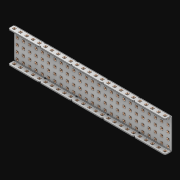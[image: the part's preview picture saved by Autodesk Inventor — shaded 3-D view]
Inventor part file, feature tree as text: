
AUTODESK INVENTOR PART (.ipt)
format: ipt  version: 2021 (Build 250183000, 183)  size: 3,581,952 bytes
history: native  units: in
note: dims shown in document units (in); Inventor stores cm internally (conversion verified against a paired STEP export)
features: extrude x176, other x175, sketch x4, thicken_offset x3, pattern_linear x3, imported_body x1
ambient origin geometry x8: Origin, YZ Plane, XZ Plane, XY Plane, X Axis, Y Axis, Z Axis, Center Point
bodies: Solid1 (feature_tree)
feature tree (362):
  thicken_offset  "Thicken1"
  thicken_offset  "Thicken2"
  thicken_offset  "Thicken3"
  pattern_linear  "Rectangular Pattern1"  Spacing1=0.001in  [1 undecoded]
  pattern_linear  "Rectangular Pattern2"  Spacing1=0.001in  [1 undecoded]
  pattern_linear  "Rectangular Pattern3"  Spacing1=0.182in  [1 undecoded]
  extrude  "Extrusion1"  Depth=0.063in TaperAngle=0.0deg
  sketch  "Sketch1"  dims[d0=0.001in]
  other  "Srf1"
  sketch  "Sketch2"  dims[d1=0.001in]
  other  "Srf2"
  sketch  "Sketch3"  dims[d2=0.001in]
  other  "Srf3"
  other  "Srf4"
  other  "Srf5"
  other  "Srf6"
  other  "Srf7"
  other  "Srf8"
  other  "Srf9"
  other  "Srf10"
  other  "Srf11"
  other  "Srf12"
  other  "Srf13"
  other  "Srf14"
  other  "Srf15"
  other  "Srf16"
  other  "Srf17"
  other  "Srf18"
  other  "Srf19"
  other  "Srf20"
  other  "Srf21"
  other  "Srf22"
  other  "Srf23"
  other  "Srf24"
  other  "Srf25"
  other  "Srf26"
  other  "Srf27"
  other  "Srf38"
  other  "Srf39"
  other  "Srf40"
  other  "Srf41"
  other  "Srf42"
  other  "Srf43"
  other  "Srf44"
  other  "Srf45"
  other  "Srf46"
  other  "Srf47"
  other  "Srf48"
  other  "Srf49"
  other  "Srf50"
  other  "Srf51"
  other  "Srf52"
  other  "Srf53"
  other  "Srf54"
  other  "Srf55"
  other  "Srf56"
  other  "Srf57"
  other  "Srf58"
  other  "Srf59"
  other  "Srf60"
  other  "Srf61"
  other  "Srf72"
  other  "Srf73"
  other  "Srf74"
  other  "Srf75"
  other  "Srf76"
  other  "Srf77"
  other  "Srf78"
  other  "Srf79"
  other  "Srf80"
  other  "Srf81"
  other  "Srf82"
  other  "Srf83"
  other  "Srf84"
  other  "Srf85"
  other  "Srf86"
  other  "Srf87"
  other  "Srf88"
  other  "Srf89"
  other  "Srf90"
  other  "Srf91"
  other  "Srf92"
  other  "Srf93"
  other  "Srf94"
  other  "Srf95"
  other  "Srf106"
  other  "Srf107"
  other  "Srf108"
  other  "Srf109"
  other  "Srf110"
  other  "Srf111"
  other  "Srf112"
  other  "Srf113"
  other  "Srf114"
  other  "Srf115"
  other  "Srf116"
  other  "Srf117"
  other  "Srf118"
  other  "Srf119"
  other  "Srf120"
  other  "Srf121"
  other  "Srf122"
  other  "Srf123"
  other  "Srf124"
  other  "Srf125"
  other  "Srf126"
  other  "Srf127"
  other  "Srf128"
  other  "Srf129"
  other  "Srf130"
  other  "Srf141"
  other  "Srf142"
  other  "Srf143"
  other  "Srf144"
  other  "Srf145"
  other  "Srf146"
  other  "Srf147"
  other  "Srf148"
  other  "Srf149"
  other  "Srf150"
  other  "Srf151"
  other  "Srf152"
  other  "Srf153"
  other  "Srf154"
  other  "Srf155"
  other  "Srf156"
  other  "Srf157"
  other  "Srf158"
  other  "Srf159"
  other  "Srf160"
  other  "Srf161"
  other  "Srf162"
  other  "Srf163"
  other  "Srf164"
  other  "Srf165"
  other  "Srf176"
  other  "Srf177"
  other  "Srf178"
  other  "Srf179"
  other  "Srf180"
  other  "Srf181"
  other  "Srf182"
  other  "Srf183"
  other  "Srf184"
  other  "Srf185"
  other  "Srf186"
  other  "Srf187"
  other  "Srf188"
  other  "Srf189"
  other  "Srf190"
  other  "Srf191"
  other  "Srf192"
  other  "Srf193"
  other  "Srf194"
  other  "Srf195"
  other  "Srf196"
  other  "Srf197"
  other  "Srf198"
  other  "Srf199"
  other  "Srf200"
  other  "Srf211"
  other  "Srf212"
  other  "Srf213"
  other  "Srf214"
  other  "Srf215"
  other  "Srf216"
  other  "Srf217"
  other  "Srf218"
  other  "Srf219"
  other  "Srf220"
  other  "Srf221"
  other  "Srf222"
  other  "Srf223"
  other  "Srf224"
  other  "Srf225"
  other  "Srf226"
  other  "Srf227"
  other  "Srf228"
  other  "Srf229"
  other  "Srf230"
  other  "Srf231"
  other  "Srf232"
  other  "Srf233"
  other  "Srf234"
  other  "Srf235"
  sketch  "Sketch4"  dims[d3=0.001in d4=0.001in d5=0.001in d6=0.182in d7=0.063in d8=0.0in d9=0.182in d10=0.063in d11=0.0in d12=0.182in d13=0.063in d14=0.0in d17=0.5in d18=9.8425in d20=0.5in d21=9.8425in d23=0.5in d24=1.9685in d26=0.5in d27=5.0in d28=0.0in]
  imported_body  "Imported1"
  extrude  "ExtrusionSrf1"  Depth=5.0in
  extrude  "ExtrusionSrf2"  Depth=0.063in TaperAngle=0.0deg
  extrude  "ExtrusionSrf3"  Depth=5.0in
  extrude  "ExtrusionSrf4"  Depth=0.063in TaperAngle=0.0deg
  extrude  "ExtrusionSrf5"  Depth=0.5in
  extrude  "ExtrusionSrf6"  Depth=5.0in
  extrude  "ExtrusionSrf7"  Depth=0.5in
  extrude  "ExtrusionSrf8"  Depth=5.0in
  extrude  "ExtrusionSrf9"  Depth=0.5in
  extrude  "ExtrusionSrf10"  Depth=0.5in
  extrude  "ExtrusionSrf11"  Depth=5.0in
  extrude  "ExtrusionSrf12"  TaperAngle=0.0deg  [1 undecoded]
  extrude  "ExtrusionSrf13"  [1 undecoded]
  extrude  "ExtrusionSrf14"  [1 undecoded]
  extrude  "ExtrusionSrf15"  [1 undecoded]
  extrude  "ExtrusionSrf16"  [1 undecoded]
  extrude  "ExtrusionSrf17"  [1 undecoded]
  extrude  "ExtrusionSrf18"  [1 undecoded]
  extrude  "ExtrusionSrf19"  [1 undecoded]
  extrude  "ExtrusionSrf20"  [1 undecoded]
  extrude  "ExtrusionSrf21"  [1 undecoded]
  extrude  "ExtrusionSrf22"  [1 undecoded]
  extrude  "ExtrusionSrf23"  [1 undecoded]
  extrude  "ExtrusionSrf24"  [1 undecoded]
  extrude  "ExtrusionSrf25"  [1 undecoded]
  extrude  "ExtrusionSrf26"  [1 undecoded]
  extrude  "ExtrusionSrf27"  [1 undecoded]
  extrude  "ExtrusionSrf38"  [1 undecoded]
  extrude  "ExtrusionSrf39"  [1 undecoded]
  extrude  "ExtrusionSrf40"  [1 undecoded]
  extrude  "ExtrusionSrf41"  [1 undecoded]
  extrude  "ExtrusionSrf42"  [1 undecoded]
  extrude  "ExtrusionSrf43"  [1 undecoded]
  extrude  "ExtrusionSrf44"  [1 undecoded]
  extrude  "ExtrusionSrf45"  [1 undecoded]
  extrude  "ExtrusionSrf46"  [1 undecoded]
  extrude  "ExtrusionSrf47"  [1 undecoded]
  extrude  "ExtrusionSrf48"  [1 undecoded]
  extrude  "ExtrusionSrf49"  [1 undecoded]
  extrude  "ExtrusionSrf50"  [1 undecoded]
  extrude  "ExtrusionSrf51"  [1 undecoded]
  extrude  "ExtrusionSrf52"  [1 undecoded]
  extrude  "ExtrusionSrf53"  [1 undecoded]
  extrude  "ExtrusionSrf54"  [1 undecoded]
  extrude  "ExtrusionSrf55"  [1 undecoded]
  extrude  "ExtrusionSrf56"  [1 undecoded]
  extrude  "ExtrusionSrf57"  [1 undecoded]
  extrude  "ExtrusionSrf58"  [1 undecoded]
  extrude  "ExtrusionSrf59"  [1 undecoded]
  extrude  "ExtrusionSrf60"  [1 undecoded]
  extrude  "ExtrusionSrf61"  [1 undecoded]
  extrude  "ExtrusionSrf72"  [1 undecoded]
  extrude  "ExtrusionSrf73"  [1 undecoded]
  extrude  "ExtrusionSrf74"  [1 undecoded]
  extrude  "ExtrusionSrf75"  [1 undecoded]
  extrude  "ExtrusionSrf76"  [1 undecoded]
  extrude  "ExtrusionSrf77"  [1 undecoded]
  extrude  "ExtrusionSrf78"  [1 undecoded]
  extrude  "ExtrusionSrf79"  [1 undecoded]
  extrude  "ExtrusionSrf80"  [1 undecoded]
  extrude  "ExtrusionSrf81"  [1 undecoded]
  extrude  "ExtrusionSrf82"  [1 undecoded]
  extrude  "ExtrusionSrf83"  [1 undecoded]
  extrude  "ExtrusionSrf84"  [1 undecoded]
  extrude  "ExtrusionSrf85"  [1 undecoded]
  extrude  "ExtrusionSrf86"  [1 undecoded]
  extrude  "ExtrusionSrf87"  [1 undecoded]
  extrude  "ExtrusionSrf88"  [1 undecoded]
  extrude  "ExtrusionSrf89"  [1 undecoded]
  extrude  "ExtrusionSrf90"  [1 undecoded]
  extrude  "ExtrusionSrf91"  [1 undecoded]
  extrude  "ExtrusionSrf92"  [1 undecoded]
  extrude  "ExtrusionSrf93"  [1 undecoded]
  extrude  "ExtrusionSrf94"  [1 undecoded]
  extrude  "ExtrusionSrf95"  [1 undecoded]
  extrude  "ExtrusionSrf106"  [1 undecoded]
  extrude  "ExtrusionSrf107"  [1 undecoded]
  extrude  "ExtrusionSrf108"  [1 undecoded]
  extrude  "ExtrusionSrf109"  [1 undecoded]
  extrude  "ExtrusionSrf110"  [1 undecoded]
  extrude  "ExtrusionSrf111"  [1 undecoded]
  extrude  "ExtrusionSrf112"  [1 undecoded]
  extrude  "ExtrusionSrf113"  [1 undecoded]
  extrude  "ExtrusionSrf114"  [1 undecoded]
  extrude  "ExtrusionSrf115"  [1 undecoded]
  extrude  "ExtrusionSrf116"  [1 undecoded]
  extrude  "ExtrusionSrf117"  [1 undecoded]
  extrude  "ExtrusionSrf118"  [1 undecoded]
  extrude  "ExtrusionSrf119"  [1 undecoded]
  extrude  "ExtrusionSrf120"  [1 undecoded]
  extrude  "ExtrusionSrf121"  [1 undecoded]
  extrude  "ExtrusionSrf122"  [1 undecoded]
  extrude  "ExtrusionSrf123"  [1 undecoded]
  extrude  "ExtrusionSrf124"  [1 undecoded]
  extrude  "ExtrusionSrf125"  [1 undecoded]
  extrude  "ExtrusionSrf126"  [1 undecoded]
  extrude  "ExtrusionSrf127"  [1 undecoded]
  extrude  "ExtrusionSrf128"  [1 undecoded]
  extrude  "ExtrusionSrf129"  [1 undecoded]
  extrude  "ExtrusionSrf130"  [1 undecoded]
  extrude  "ExtrusionSrf141"  [1 undecoded]
  extrude  "ExtrusionSrf142"  [1 undecoded]
  extrude  "ExtrusionSrf143"  [1 undecoded]
  extrude  "ExtrusionSrf144"  [1 undecoded]
  extrude  "ExtrusionSrf145"  [1 undecoded]
  extrude  "ExtrusionSrf146"  [1 undecoded]
  extrude  "ExtrusionSrf147"  [1 undecoded]
  extrude  "ExtrusionSrf148"  [1 undecoded]
  extrude  "ExtrusionSrf149"  [1 undecoded]
  extrude  "ExtrusionSrf150"  [1 undecoded]
  extrude  "ExtrusionSrf151"  [1 undecoded]
  extrude  "ExtrusionSrf152"  [1 undecoded]
  extrude  "ExtrusionSrf153"  [1 undecoded]
  extrude  "ExtrusionSrf154"  [1 undecoded]
  extrude  "ExtrusionSrf155"  [1 undecoded]
  extrude  "ExtrusionSrf156"  [1 undecoded]
  extrude  "ExtrusionSrf157"  [1 undecoded]
  extrude  "ExtrusionSrf158"  [1 undecoded]
  extrude  "ExtrusionSrf159"  [1 undecoded]
  extrude  "ExtrusionSrf160"  [1 undecoded]
  extrude  "ExtrusionSrf161"  [1 undecoded]
  extrude  "ExtrusionSrf162"  [1 undecoded]
  extrude  "ExtrusionSrf163"  [1 undecoded]
  extrude  "ExtrusionSrf164"  [1 undecoded]
  extrude  "ExtrusionSrf165"  [1 undecoded]
  extrude  "ExtrusionSrf176"  [1 undecoded]
  extrude  "ExtrusionSrf177"  [1 undecoded]
  extrude  "ExtrusionSrf178"  [1 undecoded]
  extrude  "ExtrusionSrf179"  [1 undecoded]
  extrude  "ExtrusionSrf180"  [1 undecoded]
  extrude  "ExtrusionSrf181"  [1 undecoded]
  extrude  "ExtrusionSrf182"  [1 undecoded]
  extrude  "ExtrusionSrf183"  [1 undecoded]
  extrude  "ExtrusionSrf184"  [1 undecoded]
  extrude  "ExtrusionSrf185"  [1 undecoded]
  extrude  "ExtrusionSrf186"  [1 undecoded]
  extrude  "ExtrusionSrf187"  [1 undecoded]
  extrude  "ExtrusionSrf188"  [1 undecoded]
  extrude  "ExtrusionSrf189"  [1 undecoded]
  extrude  "ExtrusionSrf190"  [1 undecoded]
  extrude  "ExtrusionSrf191"  [1 undecoded]
  extrude  "ExtrusionSrf192"  [1 undecoded]
  extrude  "ExtrusionSrf193"  [1 undecoded]
  extrude  "ExtrusionSrf194"  [1 undecoded]
  extrude  "ExtrusionSrf195"  [1 undecoded]
  extrude  "ExtrusionSrf196"  [1 undecoded]
  extrude  "ExtrusionSrf197"  [1 undecoded]
  extrude  "ExtrusionSrf198"  [1 undecoded]
  extrude  "ExtrusionSrf199"  [1 undecoded]
  extrude  "ExtrusionSrf200"  [1 undecoded]
  extrude  "ExtrusionSrf211"  [1 undecoded]
  extrude  "ExtrusionSrf212"  [1 undecoded]
  extrude  "ExtrusionSrf213"  [1 undecoded]
  extrude  "ExtrusionSrf214"  [1 undecoded]
  extrude  "ExtrusionSrf215"  [1 undecoded]
  extrude  "ExtrusionSrf216"  [1 undecoded]
  extrude  "ExtrusionSrf217"  [1 undecoded]
  extrude  "ExtrusionSrf218"  [1 undecoded]
  extrude  "ExtrusionSrf219"  [1 undecoded]
  extrude  "ExtrusionSrf220"  [1 undecoded]
  extrude  "ExtrusionSrf221"  [1 undecoded]
  extrude  "ExtrusionSrf222"  [1 undecoded]
  extrude  "ExtrusionSrf223"  [1 undecoded]
  extrude  "ExtrusionSrf224"  [1 undecoded]
  extrude  "ExtrusionSrf225"  [1 undecoded]
  extrude  "ExtrusionSrf226"  [1 undecoded]
  extrude  "ExtrusionSrf227"  [1 undecoded]
  extrude  "ExtrusionSrf228"  [1 undecoded]
  extrude  "ExtrusionSrf229"  [1 undecoded]
  extrude  "ExtrusionSrf230"  [1 undecoded]
  extrude  "ExtrusionSrf231"  [1 undecoded]
  extrude  "ExtrusionSrf232"  [1 undecoded]
  extrude  "ExtrusionSrf233"  [1 undecoded]
  extrude  "ExtrusionSrf234"  [1 undecoded]
  extrude  "ExtrusionSrf235"  [1 undecoded]
note: 167 required parameter values undecoded (feature->parameter linkage not recoverable at this tier; creation-order binding heuristic only, values carry confidence <= 0.55)
